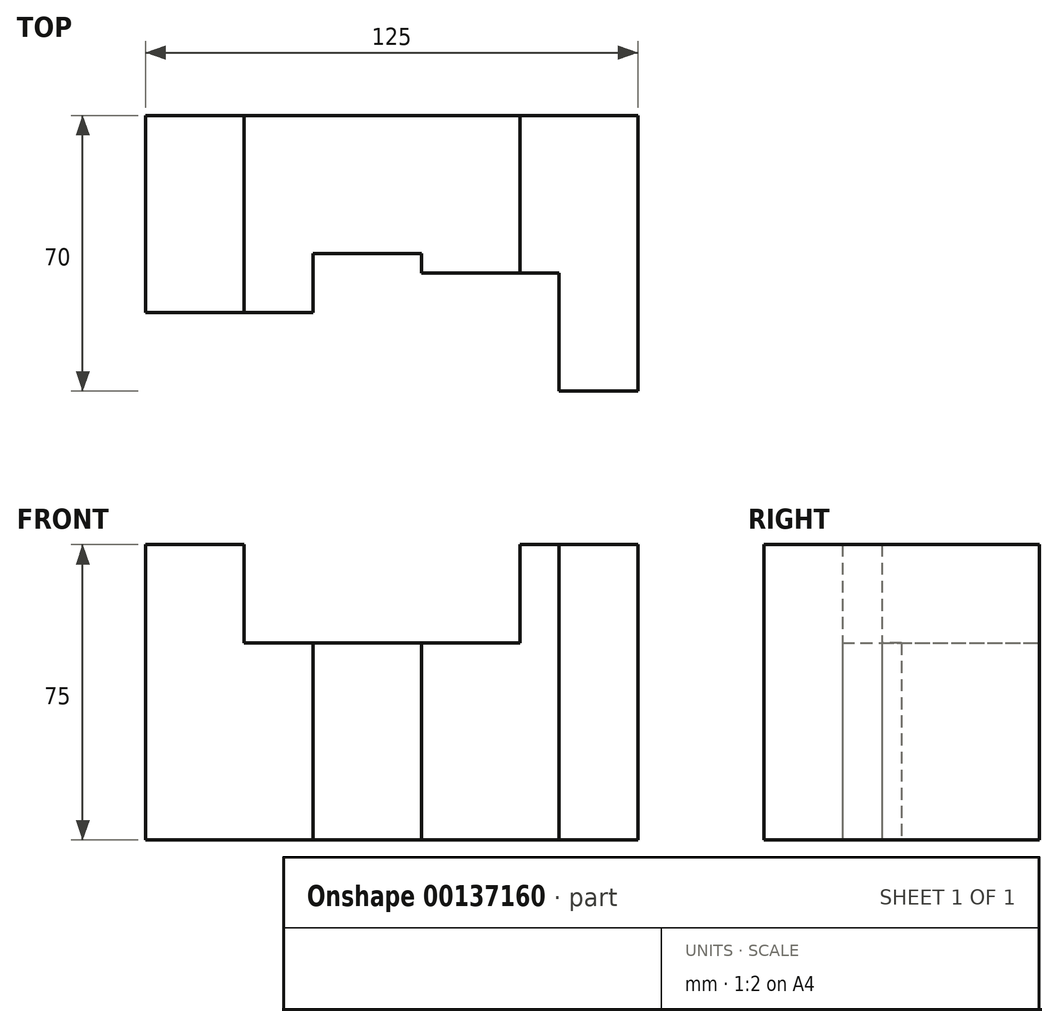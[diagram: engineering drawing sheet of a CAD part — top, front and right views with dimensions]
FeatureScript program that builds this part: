
annotation { "Feature Type Name" : "Feature", "Feature Type Description" : "" }
export const myFeature = defineFeature(function(context is Context, id is Id, definition is map)
    precondition{}
    {
        {
            var Q0;
            Q0=qCreatedBy(makeId("Top.planeOp"),FACE);
            var sketch = newSketch(context, id + "F0", { "sketchPlane" : qUnion([Q0])});
            skLineSegment(sketch, "E0", {"start": v(0, 0) * mm, "end": v(0, -50) * mm});
            skLineSegment(sketch, "E1", {"start": v(0, -50) * mm, "end": v(25, -50) * mm});
            skLineSegment(sketch, "E2", {"start": v(25, -50) * mm, "end": v(25, 0) * mm});
            skLineSegment(sketch, "E3", {"start": v(25, 0) * mm, "end": v(0, 0) * mm});
            skLineSegment(sketch, "E4", {"start": v(25, -50) * mm, "end": v(42.5, -50) * mm});
            skLineSegment(sketch, "E5", {"start": v(42.5, -50) * mm, "end": v(42.5, -35) * mm});
            skLineSegment(sketch, "E6", {"start": v(42.5, -35) * mm, "end": v(70, -35) * mm});
            skLineSegment(sketch, "E7", {"start": v(70, -35) * mm, "end": v(70, -40) * mm});
            skLineSegment(sketch, "E8", {"start": v(70, -40) * mm, "end": v(95, -40) * mm});
            skLineSegment(sketch, "E9", {"start": v(95, -40) * mm, "end": v(105, -40) * mm});
            skLineSegment(sketch, "E10", {"start": v(105, -40) * mm, "end": v(105, -70) * mm});
            skLineSegment(sketch, "E11", {"start": v(105, -70) * mm, "end": v(125, -70) * mm});
            skLineSegment(sketch, "E12", {"start": v(125, -70) * mm, "end": v(125, 0) * mm});
            skLineSegment(sketch, "E13", {"start": v(125, 0) * mm, "end": v(25, 0) * mm});
            skLineSegment(sketch, "E14", {"start": v(95, -40) * mm, "end": v(95, 0) * mm});
            skSolve(sketch);
        }
        {
            var Q0;
            {var subQ0=sQuery(id+"F0.wireOp",EDGE,"E2");Q0=makeQuery(id+"F0.imprint","IMPRINT",FACE,{"disambiguationData":[TD([[makeQuery(id+"F0.imprint","IMPRINT",EDGE,{"derivedFrom":subQ0}),-1.0]])]});}
            var Q1;
            {var subQ0=sQuery(id+"F0.wireOp",EDGE,"E2");Q1=makeQuery(id+"F0.imprint","IMPRINT",FACE,{"disambiguationData":[TD([[makeQuery(id+"F0.imprint","IMPRINT",EDGE,{"derivedFrom":subQ0}),-1.0]])]});}
            extrude(context, id + "F1", {"entities" : qUnion([Q0, Q1]), "depth" : 50 * mm});
        }
        {
            var Q0;
            Q0=makeQuery(id+"F0.imprint","IMPRINT",FACE,{"disambiguationData":[TD([[makeQuery(id+"F0.imprint","IMPRINT",EDGE,{"derivedFrom":sQuery(id+"F0.wireOp",EDGE,"E0")}),1.0]])]});
            extrude(context, id + "F2", {"entities" : qUnion([Q0]), "operationType" : NewBodyOperationType.ADD, "depth" : 75 * mm});
        }
        {
            var Q0;
            Q0=makeQuery(id+"F0.imprint","IMPRINT",FACE,{"disambiguationData":[TD([[makeQuery(id+"F0.imprint","IMPRINT",EDGE,{"derivedFrom":sQuery(id+"F0.wireOp",EDGE,"E9")}),1.0]])]});
            extrude(context, id + "F3", {"entities" : qUnion([Q0]), "operationType" : NewBodyOperationType.ADD, "depth" : 75 * mm});
        }
    });
